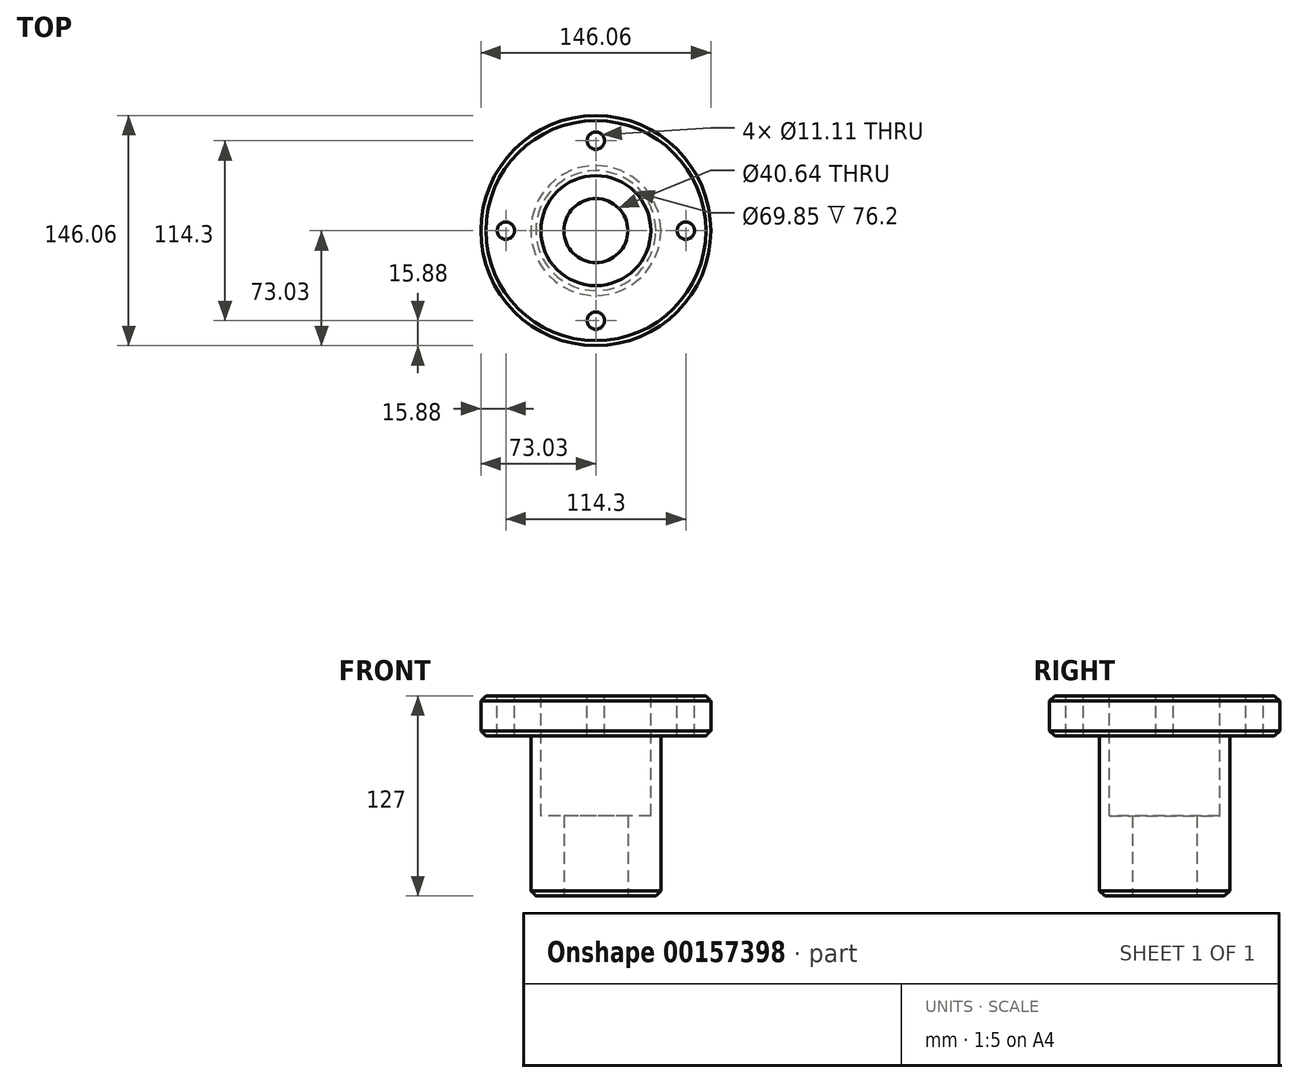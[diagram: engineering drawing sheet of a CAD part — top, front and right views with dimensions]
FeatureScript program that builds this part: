
annotation { "Feature Type Name" : "Feature", "Feature Type Description" : "" }
export const myFeature = defineFeature(function(context is Context, id is Id, definition is map)
    precondition{}
    {
        {
            var Q0;
            Q0=qCreatedBy(makeId("Top.planeOp"),FACE);
            var sketch = newSketch(context, id + "F0", { "sketchPlane" : qUnion([Q0])});
            skCircle(sketch, "E0", {"center": v(0, 0) * mm, "radius": 73.03 * mm});
            skSolve(sketch);
        }
        {
            var Q0;
            Q0 = qSketchRegion(id + "F0", true);
            extrude(context, id + "F1", {"entities" : qUnion([Q0]), "depth" : 25.4 * mm});
        }
        {
            var Q0;
            Q0=makeQuery(id+"F1.opExtrude","CAP_FACE",FACE,{"disambiguationData":[OSD([sQuery(id+"F0.wireOp",EDGE,"E0")])],"isStart":true});
            var sketch = newSketch(context, id + "F2", { "sketchPlane" : qUnion([Q0])});
            skCircle(sketch, "E1", {"center": v(0, 0) * mm, "radius": 41.28 * mm});
            skSolve(sketch);
        }
        {
            var Q0;
            Q0 = qSketchRegion(id + "F2", true);
            extrude(context, id + "F3", {"entities" : qUnion([Q0]), "operationType" : NewBodyOperationType.ADD, "depth" : 101.6 * mm});
        }
        {
            var Q0;
            Q0=makeQuery(id+"F3.opExtrude","CAP_FACE",FACE,{"disambiguationData":[OSD([sQuery(id+"F2.wireOp",EDGE,"E1")])],"isStart":false});
            var sketch = newSketch(context, id + "F4", { "sketchPlane" : qUnion([Q0])});
            skCircle(sketch, "E2", {"center": v(0, 0) * mm, "radius": 20.32 * mm});
            skSolve(sketch);
        }
        {
            var Q0;
            Q0 = qSketchRegion(id + "F4", true);
            extrude(context, id + "F5", {"entities" : qUnion([Q0]), "operationType" : NewBodyOperationType.REMOVE, "endBound" : BoundingType.THROUGH_ALL, "oppositeDirection" : true, "depth" : 25.4 * mm});
        }
        {
            var Q0;
            Q0=makeQuery(id+"F1.opExtrude","CAP_FACE",FACE,{"disambiguationData":[OSD([sQuery(id+"F0.wireOp",EDGE,"E0")])],"isStart":false});
            var sketch = newSketch(context, id + "F6", { "sketchPlane" : qUnion([Q0])});
            skCircle(sketch, "E3", {"center": v(-57.15, 0) * mm, "radius": 5.56 * mm});
            skCircle(sketch, "E4", {"center": v(0, 57.15) * mm, "radius": 5.56 * mm});
            skCircle(sketch, "E5", {"center": v(57.15, 0) * mm, "radius": 5.56 * mm});
            skCircle(sketch, "E6", {"center": v(0, -57.15) * mm, "radius": 5.56 * mm});
            skCircle(sketch, "E7", {"center": v(0, 0) * mm, "radius": 34.93 * mm});
            skSolve(sketch);
        }
        {
            var Q0;
            Q0 = qSketchRegion(id + "F6", true);
            extrude(context, id + "F7", {"entities" : qUnion([Q0]), "operationType" : NewBodyOperationType.REMOVE, "oppositeDirection" : true, "depth" : 76.2 * mm});
        }
        {
            var Q0;
            Q0=makeQuery(id+"F1.opExtrude","CAP_EDGE",EDGE,{"disambiguationData":[OSD([sQuery(id+"F0.wireOp",EDGE,"E0")])],"isStart":false});
            var Q1;
            Q1=makeQuery(id+"F1.opExtrude","CAP_EDGE",EDGE,{"disambiguationData":[OSD([sQuery(id+"F0.wireOp",EDGE,"E0")])],"isStart":true});
            var Q2;
            Q2=makeQuery(id+"F3.opExtrude","CAP_EDGE",EDGE,{"disambiguationData":[OSD([sQuery(id+"F2.wireOp",EDGE,"E1")])],"isStart":false});
            chamfer(context, id + "F8", {"entities" : qUnion([Q0, Q1, Q2]), "width" : 3.17 * mm, "tangentPropagation" : true});
        }
    });
